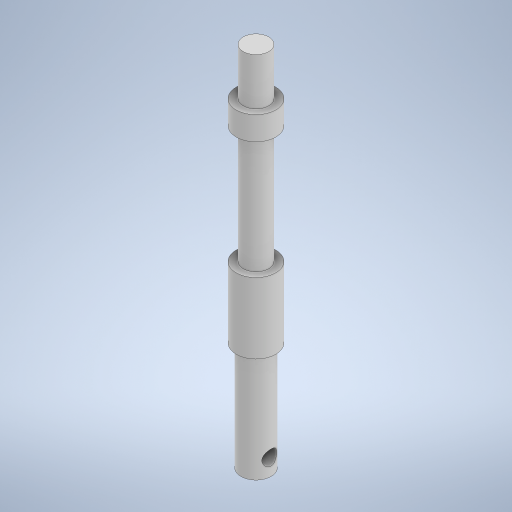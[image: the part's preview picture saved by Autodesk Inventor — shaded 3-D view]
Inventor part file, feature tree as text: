
AUTODESK INVENTOR PART (.ipt)
format: ipt  version: 2023 (Build 270158000, 158)  size: 265,216 bytes
history: native  units: in
note: dims shown in document units (in); Inventor stores cm internally (conversion verified against a paired STEP export)
features: sketch x1, revolve x1, extrude x1
ambient origin geometry x8: Origin, YZ Plane, XZ Plane, XY Plane, X Axis, Y Axis, Z Axis, Center Point
bodies: Solid1 (feature_tree)
feature tree (3):
  sketch  "Sketch1"  dims[d5=0.4in d9=0.032in d10=0.042in d11=0.027in d12=0.042in d13=0.027in d14=0.05in d15=0.25in d16=0.15in d17=0.23in d18=0.1in d19=90.0deg d20=0.62in d21=0.0312in d22=1.0in d23=0.0in]
  revolve  "Revolution1"  [1 undecoded]
  extrude  "Extrusion1"  Depth=0.23in
note: 1 required parameter value undecoded (feature->parameter linkage not recoverable at this tier; creation-order binding heuristic only, values carry confidence <= 0.55)
